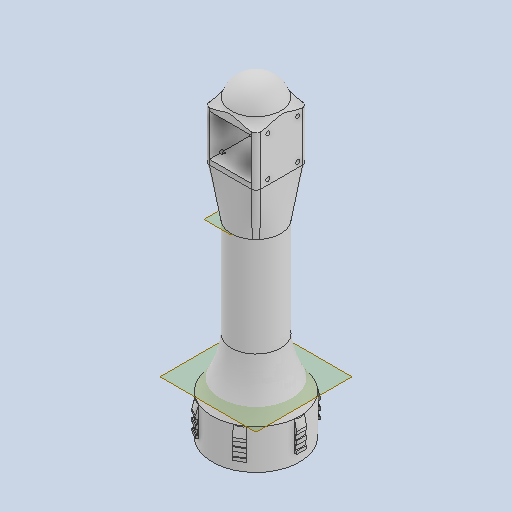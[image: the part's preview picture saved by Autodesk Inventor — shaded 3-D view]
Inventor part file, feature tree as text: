
AUTODESK INVENTOR PART (.ipt)
format: ipt  version: 2022.3 (Build 263350000, 350)  size: 610,304 bytes
history: native  units: mm
features: sketch x16, extrude x11, other x6, revolve x3, hole x3, plane x2, fillet x2, loft x1, pattern_circular x1, projected_geometry x1
ambient origin geometry x8: Origin, YZ Plane, XZ Plane, XY Plane, X Axis, Y Axis, Z Axis, Center Point
bodies: Solid1 (feature_tree)
feature tree (46):
  other  "{BB8FE430-83BF-418D-8DF9-9B323D3DB9B9}"
  extrude  "Extrusion1"  Depth=4.0mm
  revolve  "Revolution1"  [1 undecoded]
  plane  "Work Plane1"
  extrude  "Extrusion2"  Depth=100.0mm
  extrude  "Extrusion3"  Depth=4.0mm
  plane  "Work Plane2"
  sketch  "Sketch5"  dims[d12=100.0mm d13=90.0deg]
  fillet  "Fillet1"  Radius=4.0mm
  loft  "Loft1"
  extrude  "Extrusion4"  Depth=5.0mm
  sketch  "Sketch11"  dims[d16=65.0mm d17=65.0mm]
  extrude  "Extrusion7"  Depth=65.0mm
  extrude  "Extrusion8"  Depth=5.0mm
  extrude  "Extrusion9"  Depth=5.0mm TaperAngle=0.0deg
  hole  "Hole2"  [1 undecoded]
  extrude  "Extrusion10"  Depth=5.0mm
  revolve  "Revolution2"  Angle=90.0deg
  fillet  "Fillet3"  [1 undecoded]
  hole  "Hole3"  [1 undecoded]
  hole  "Hole4"  [1 undecoded]
  sketch  "Sketch18"  dims[d55=4.5mm d56=5.0mm d57=0.0mm]
  extrude  "Extrusion11"  Depth=45.0mm
  extrude  "Extrusion12"  Depth=42.0mm TaperAngle=0.0deg
  extrude  "Extrusion13"  Depth=31.0mm
  pattern_circular  "Circular Pattern2"  [2 undecoded]
  revolve  "Revolution4"  [1 undecoded]
  other  "Spur Gear Teeth1"
  other  "Spur Gear Teeth2"
  sketch  "Sketch1"  dims[d0=80.0mm d1=4.0mm]
  sketch  "Sketch2"  dims[d2=40.0mm d3=0.0mm d4=88.0mm]
  sketch  "Sketch3"  dims[d5=50.0mm d8=100.0mm]
  sketch  "Sketch4"  dims[d9=25.0mm d10=150.0mm d11=4.0mm]
  other  "Edges1"
  sketch  "Sketch7"  dims[d14=-52.5mm d15=5.0mm]
  projected_geometry  "Projected Loop2"
  sketch  "Sketch12"  dims[d18=5.0mm d19=15.0mm]
  sketch  "Sketch13"  dims[d20=10.0mm d21=5.0mm d22=0.0mm]
  sketch  "Sketch14"  dims[d23=52.0mm d24=52.0mm]
  sketch  "Sketch15"  dims[d25=5.0mm d26=0.0mm d27=50.0mm]
  sketch  "Sketch16"  dims[d28=5.0mm d29=0.0mm d30=90.0deg d31=0.0mm d32=90.0deg]
  sketch  "Sketch17"  dims[d33=100.0mm d34=0.0mm d54=5.0mm]
  sketch  "Sketch19"  dims[d58=45.0mm d59=0.0mm d60=45.0mm]
  sketch  "Sketch20"  dims[d61=22.0mm d62=42.0mm d63=0.0mm d64=31.0mm d65=31.0mm d66=2.4mm d67=6.0mm d68=4.0mm d69=2.0mm d70=90.0deg d71=5.0mm d72=0.0mm d73=3.0mm d74=0.0mm d75=26.0mm d76=26.0mm d77=90.0deg d78=10.0mm d79=0.0mm d80=5.0mm d81=5.0mm d82=5.0mm d83=5.068mm d84=3.4mm d85=6.0mm d86=4.1mm d87=5.1mm d88=90.0deg d89=2.2mm d90=0.0mm d91=5.0mm d92=5.0mm d93=5.0mm d94=5.068mm d95=3.4mm d96=6.0mm d97=4.1mm d98=5.1mm d99=90.0deg d100=2.2mm d101=0.0mm d102=30.0mm d103=40.0mm d104=30.0mm d105=40.0mm d106=4.0mm d107=10.0mm d108=30.0mm d109=0.0mm d110=10.0mm d111=30.0mm d112=0.0mm d113=1.0mm d114=10.0mm d115=1.0mm d116=3.0mm d117=1.0mm d118=5.0mm d119=1.0mm d120=4.0mm d121=1.0mm d122=5.0mm d123=10.0mm d124=90.0deg d131=10.0mm d132=0.0mm d133=1.0mm d134=3.0mm d135=60.0mm d136=360.0deg d138=2.0mm d139=5.0mm d140=2.0mm d141=5.0mm d142=90.0deg d125=0.872665mm d126=0.872665mm d137=14.3117mm]
  other  "Spur Gear1"
  other  "Spur Gear12"
note: 8 required parameter values undecoded (feature->parameter linkage not recoverable at this tier; creation-order binding heuristic only, values carry confidence <= 0.55)